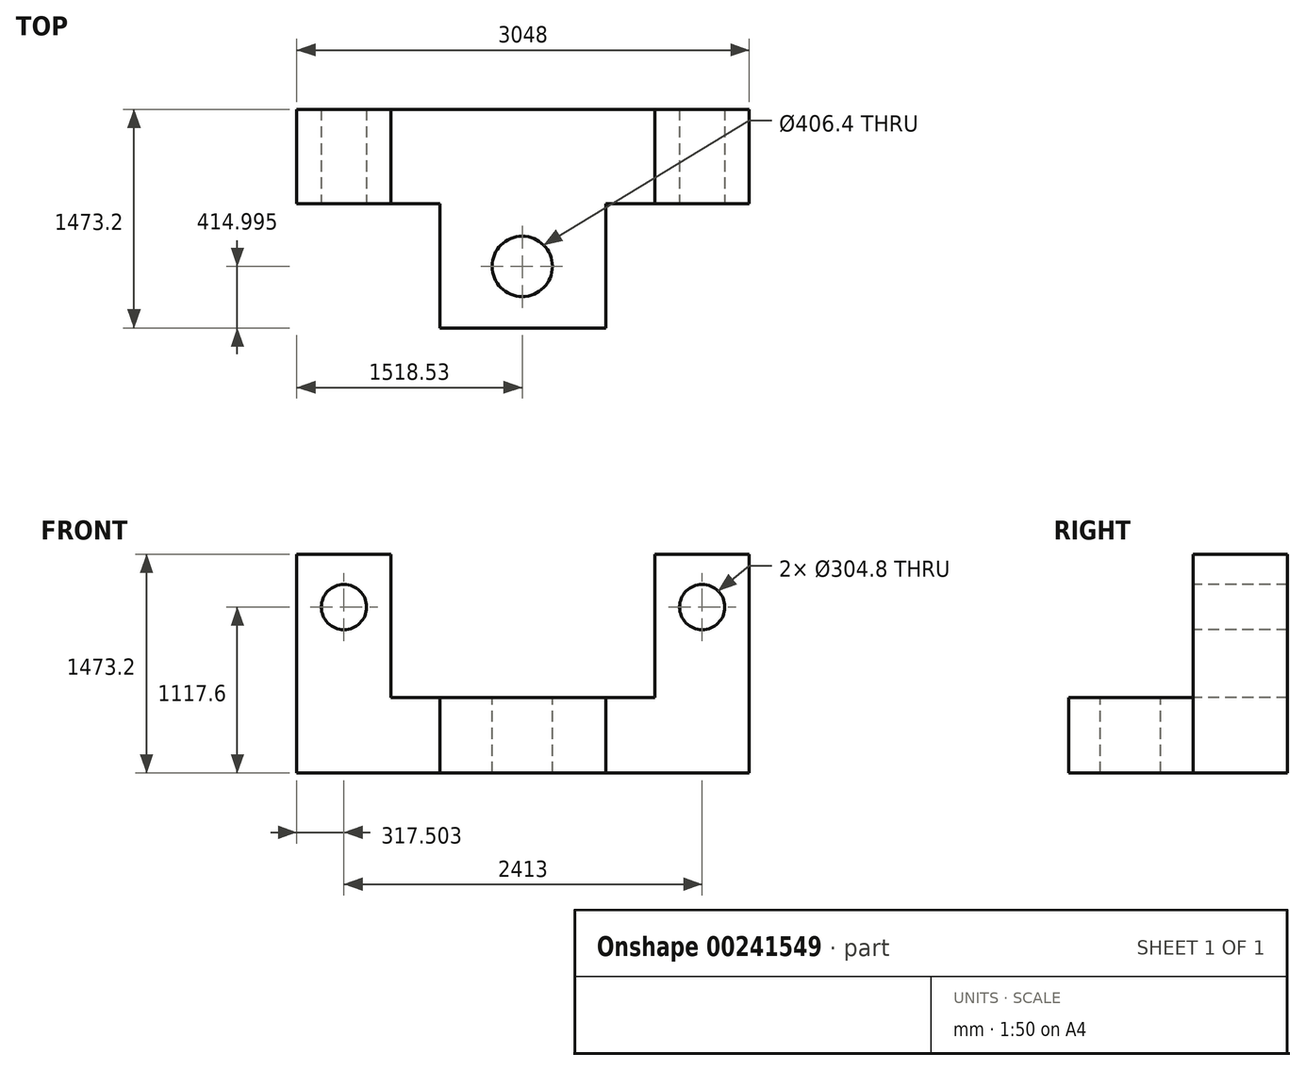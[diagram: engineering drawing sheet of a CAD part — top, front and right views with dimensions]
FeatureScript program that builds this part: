
annotation { "Feature Type Name" : "Feature", "Feature Type Description" : "" }
export const myFeature = defineFeature(function(context is Context, id is Id, definition is map)
    precondition{}
    {
        {
            var Q0;
            Q0=qCreatedBy(makeId("Front.planeOp"),FACE);
            var sketch = newSketch(context, id + "F0", { "sketchPlane" : qUnion([Q0])});
            skLineSegment(sketch, "E0", {"start": v(-1518.53, -28.4) * mm, "end": v(1529.47, -28.4) * mm});
            skLineSegment(sketch, "E1", {"start": v(-1518.53, -28.4) * mm, "end": v(-1518.53, 1444.8) * mm});
            skLineSegment(sketch, "E2", {"start": v(-1518.53, 1444.8) * mm, "end": v(1529.47, 1444.8) * mm});
            skLineSegment(sketch, "E3", {"start": v(1529.47, -28.4) * mm, "end": v(1529.47, 1444.8) * mm});
            skSolve(sketch);
        }
        {
            var Q0;
            Q0 = qSketchRegion(id + "F0", true);
            extrude(context, id + "F1", {"entities" : qUnion([Q0]), "depth" : 1473.2 * mm});
        }
        {
            var Q0;
            Q0=makeQuery(id+"F1.opExtrude","SWEPT_FACE",FACE,{"disambiguationData":[OSD([sQuery(id+"F0.wireOp",EDGE,"E2")])]});
            var sketch = newSketch(context, id + "F2", { "sketchPlane" : qUnion([Q0])});
            skLineSegment(sketch, "E4", {"start": v(1529.47, -1473.2) * mm, "end": v(1529.47, -635) * mm});
            skLineSegment(sketch, "E5", {"start": v(1529.47, -1473.2) * mm, "end": v(564.27, -1473.2) * mm});
            skLineSegment(sketch, "E6", {"start": v(564.27, -1473.2) * mm, "end": v(564.27, -635) * mm});
            skLineSegment(sketch, "E7", {"start": v(1529.47, -635) * mm, "end": v(564.27, -635) * mm});
            skLineSegment(sketch, "E8", {"start": v(-1518.53, -1473.2) * mm, "end": v(-1518.53, -635) * mm});
            skLineSegment(sketch, "E9", {"start": v(-1518.53, -1473.2) * mm, "end": v(-553.33, -1473.2) * mm});
            skLineSegment(sketch, "E10", {"start": v(-1518.53, -635) * mm, "end": v(-553.33, -635) * mm});
            skLineSegment(sketch, "E11", {"start": v(-553.33, -635) * mm, "end": v(-553.33, -1473.2) * mm});
            skSolve(sketch);
        }
        {
            var Q0;
            Q0 = qSketchRegion(id + "F2", true);
            extrude(context, id + "F3", {"entities" : qUnion([Q0]), "operationType" : NewBodyOperationType.REMOVE, "oppositeDirection" : true, "depth" : 1473.2 * mm});
        }
        {
            var Q0;
            Q0=makeQuery(id+"F1.opExtrude","SWEPT_FACE",FACE,{"disambiguationData":[OSD([sQuery(id+"F0.wireOp",EDGE,"E2")])]});
            var sketch = newSketch(context, id + "F4", { "sketchPlane" : qUnion([Q0])});
            skLineSegment(sketch, "E12", {"start": v(-1518.53, 0) * mm, "end": v(-883.53, 0) * mm});
            skLineSegment(sketch, "E13", {"start": v(1529.47, 0) * mm, "end": v(894.47, 0) * mm});
            skLineSegment(sketch, "E14", {"start": v(894.47, 0) * mm, "end": v(894.47, -635) * mm});
            skLineSegment(sketch, "E15", {"start": v(894.47, -635) * mm, "end": v(564.27, -635) * mm});
            skLineSegment(sketch, "E16", {"start": v(564.27, -635) * mm, "end": v(564.27, -1473.2) * mm});
            skLineSegment(sketch, "E17", {"start": v(564.27, -1473.2) * mm, "end": v(-553.33, -1473.2) * mm});
            skLineSegment(sketch, "E18", {"start": v(-553.33, -1473.2) * mm, "end": v(-553.33, -635) * mm});
            skLineSegment(sketch, "E19", {"start": v(-883.53, 0) * mm, "end": v(-883.53, -635) * mm});
            skLineSegment(sketch, "E20", {"start": v(-883.53, -635) * mm, "end": v(-553.33, -635) * mm});
            skLineSegment(sketch, "E21", {"start": v(-883.53, 0) * mm, "end": v(894.47, 0) * mm});
            skSolve(sketch);
        }
        {
            var Q0;
            Q0=makeQuery(id+"F4.imprint","IMPRINT",FACE,{"disambiguationData":[TD([[makeQuery(id+"F4.imprint","IMPRINT",EDGE,{"derivedFrom":sQuery(id+"F4.wireOp",EDGE,"E14")}),-1.0]])]});
            extrude(context, id + "F5", {"entities" : qUnion([Q0]), "operationType" : NewBodyOperationType.REMOVE, "oppositeDirection" : true, "depth" : 965.2 * mm});
        }
        {
            var Q0;
            Q0=makeQuery(id+"F3.boolean.opBoolean","COPY",FACE,{"derivedFrom":makeQuery(id+"F3.opExtrude","SWEPT_FACE",FACE,{"disambiguationData":[OSD([sQuery(id+"F2.wireOp",EDGE,"E10")])]})});
            var sketch = newSketch(context, id + "F6", { "sketchPlane" : qUnion([Q0])});
            skPoint(sketch, "E22.startSnap0", {"position": v(-1201.03, 1444.8) * mm});
            skCircle(sketch, "E23", {"center": v(-1201.03, 1089.2) * mm, "radius": 152.4 * mm});
            skSolve(sketch);
        }
        {
            var Q0;
            Q0 = qSketchRegion(id + "F6", true);
            extrude(context, id + "F7", {"entities" : qUnion([Q0]), "operationType" : NewBodyOperationType.REMOVE, "oppositeDirection" : true, "depth" : 635 * mm});
        }
        {
            var Q0;
            Q0=makeQuery(id+"F3.boolean.opBoolean","COPY",FACE,{"derivedFrom":makeQuery(id+"F3.opExtrude","SWEPT_FACE",FACE,{"disambiguationData":[OSD([sQuery(id+"F2.wireOp",EDGE,"E7")])]})});
            var sketch = newSketch(context, id + "F8", { "sketchPlane" : qUnion([Q0])});
            skPoint(sketch, "E24.startSnap0", {"position": v(1211.97, 1444.8) * mm});
            skCircle(sketch, "E25", {"center": v(1211.97, 1089.2) * mm, "radius": 152.4 * mm});
            skSolve(sketch);
        }
        {
            var Q0;
            Q0 = qSketchRegion(id + "F8", true);
            extrude(context, id + "F9", {"entities" : qUnion([Q0]), "operationType" : NewBodyOperationType.REMOVE, "oppositeDirection" : true, "depth" : 635 * mm});
        }
        {
            var Q0;
            Q0=makeQuery(id+"F5.boolean.opBoolean","COPY",FACE,{"derivedFrom":makeQuery(id+"F5.opExtrude","CAP_FACE",FACE,{"disambiguationData":[OSD([sQuery(id+"F4.wireOp",EDGE,"E14"),sQuery(id+"F4.wireOp",EDGE,"E15"),sQuery(id+"F4.wireOp",EDGE,"E16"),sQuery(id+"F4.wireOp",EDGE,"E17"),sQuery(id+"F4.wireOp",EDGE,"E18"),sQuery(id+"F4.wireOp",EDGE,"E19"),sQuery(id+"F4.wireOp",EDGE,"E20"),sQuery(id+"F4.wireOp",EDGE,"E21")])],"isStart":false})});
            var sketch = newSketch(context, id + "F10", { "sketchPlane" : qUnion([Q0])});
            skCircle(sketch, "E26", {"center": v(0, -1058.2) * mm, "radius": 203.2 * mm});
            skSolve(sketch);
        }
        {
            var Q0;
            Q0 = qSketchRegion(id + "F10", true);
            extrude(context, id + "F11", {"entities" : qUnion([Q0]), "operationType" : NewBodyOperationType.REMOVE, "oppositeDirection" : true, "depth" : 508 * mm});
        }
    });
